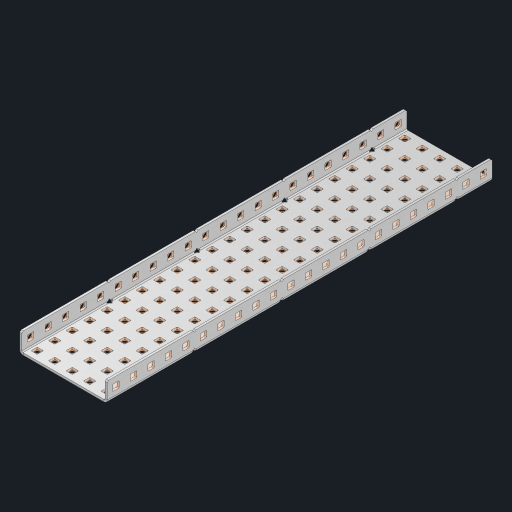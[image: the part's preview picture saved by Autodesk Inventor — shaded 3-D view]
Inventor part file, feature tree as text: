
AUTODESK INVENTOR PART (.ipt)
format: ipt  version: 2023 (Build 270158000, 158)  size: 1,768,448 bytes
history: native  units: in
note: dims shown in document units (in); Inventor stores cm internally (conversion verified against a paired STEP export)
features: other x159, extrude x153, sheet_metal_op x10, sketch x8, mirror x1, pattern_linear x1, chamfer x1
ambient origin geometry x8: Origin, YZ Plane, XZ Plane, XY Plane, X Axis, Y Axis, Z Axis, Center Point
bodies: Solid1 (feature_tree), Body (feature_tree)
feature tree (333):
  other  "Flange Pattern Plane"
  sheet_metal_op  "Flange Pattern"
  sheet_metal_op  "Body Pattern"
  other  "Arc Length"
  mirror  "Notch Mirror"
  pattern_linear  "Notch Pattern"  Spacing1=0.25in  [1 undecoded]
  chamfer  "End Chamfer"
  extrude  "Half Cut"  Depth=0.0625in
  sketch  "Sketch1"  dims[d0=2.5in]
  other  "Plate1"
  sketch  "Sketch2"  dims[d1=11.0in]
  other  "Plate2"
  sheet_metal_op  "Bend1"
  sheet_metal_op  "Corner1"
  sketch  "Sketch3"  dims[d2=0.0625in]
  other  "Flange Pattern Sketch"
  sketch  "Sketch7"  dims[d3=0.0625in]
  other  "Srf1"
  other  "Srf2"
  sketch  "Sketch8"  dims[d4=0.0312in]
  sketch  "Sketch9"  dims[d5=0.125in]
  other  "Srf91"
  sheet_metal_op  "Body Pattern Sketch"
  other  "Srf92"
  sketch  "Sketch13"  dims[d6=0.0625in]
  sketch  "Sketch14"  dims[d7=0.5in d8=90.0deg d9=0.0312in d10=0.25in d11=0.0625in d12=0.0625in d16=0.182in d17=0.02in d18=0.0625in d19=0.0in d20=0.25in d21=0.25in d46=0.172in d47=1.0in d48=0.0in d49=0.182in d50=0.02in d51=0.25in d52=0.25in d53=0.0625in d54=0.0in d55=0.172in d56=1.0in d57=0.0in d60=8.6614in d62=0.5in d63=1.9685in d65=0.5in d85=0.1473in d86=0.1782in d88=0.04in d89=0.0625in d90=0.0in d91=0.04in d92=0.0491in d95=2.5in d96=0.04in d97=0.25in d98=45.0deg d101=0.0in d102=2.497in d131=2.5in d132=8.6614in d134=0.5in d139=0.5in]
  other  "Srf856"
  other  "Srf1310"
  other  "Srf1311"
  other  "Srf1312"
  other  "Srf1376"
  other  "Srf1377"
  other  "Srf1728"
  other  "Srf1755"
  other  "Srf1878"
  other  "Srf1879"
  other  "Srf1880"
  other  "Srf1881"
  other  "Srf1882"
  other  "Srf1883"
  other  "Srf1884"
  other  "Srf1885"
  other  "Srf1886"
  other  "Srf1887"
  other  "Srf1888"
  other  "Srf1889"
  other  "Srf1890"
  other  "Srf1891"
  other  "Srf1892"
  other  "Srf1893"
  other  "Srf1894"
  other  "Srf1895"
  other  "Srf1896"
  other  "Srf1897"
  other  "Srf1898"
  other  "Srf1899"
  other  "Srf1900"
  other  "Srf1901"
  other  "Srf1902"
  other  "Srf1903"
  other  "Srf1904"
  other  "Srf1905"
  other  "Srf1906"
  other  "Srf1942"
  other  "Srf1943"
  other  "Srf1944"
  other  "Srf1945"
  other  "Srf1946"
  other  "Srf1947"
  other  "Srf1948"
  other  "Srf1949"
  other  "Srf1950"
  other  "Srf1951"
  other  "Srf1952"
  other  "Srf1953"
  other  "Srf1954"
  other  "Srf1955"
  other  "Srf1956"
  other  "Srf1957"
  other  "Srf1958"
  other  "Srf1959"
  other  "Srf1960"
  other  "Srf1961"
  other  "Srf1962"
  other  "Srf1963"
  other  "Srf1964"
  other  "Srf1965"
  other  "Srf1966"
  other  "Srf1967"
  other  "Srf1968"
  other  "Srf1969"
  other  "Srf1970"
  other  "Srf2111"
  other  "Srf2112"
  other  "Srf2113"
  other  "Srf2114"
  other  "Srf2115"
  other  "Srf2116"
  other  "Srf2117"
  other  "Srf2118"
  other  "Srf2119"
  other  "Srf2146"
  other  "Srf2147"
  other  "Srf2148"
  other  "Srf2149"
  other  "Srf2150"
  other  "Srf2151"
  other  "Srf2152"
  other  "Srf2153"
  other  "Srf2154"
  other  "Srf2155"
  other  "Srf2156"
  other  "Srf2157"
  other  "Srf2158"
  other  "Srf2159"
  other  "Srf2160"
  other  "Srf2161"
  other  "Srf2162"
  other  "Srf2163"
  other  "Srf2164"
  other  "Srf2165"
  other  "Srf2166"
  other  "Srf2167"
  other  "Srf2168"
  other  "Srf2169"
  other  "Srf2170"
  other  "Srf2171"
  other  "Srf2172"
  other  "Srf2173"
  other  "Srf2174"
  other  "Srf2175"
  other  "Srf2176"
  other  "Srf2177"
  other  "Srf2178"
  other  "Srf2179"
  other  "Srf2180"
  other  "Srf2181"
  other  "Srf2182"
  other  "Srf2183"
  other  "Srf2184"
  other  "Srf2185"
  other  "Srf2186"
  other  "Srf2187"
  other  "Srf2188"
  other  "Srf2189"
  other  "Srf2190"
  other  "Srf2191"
  other  "Srf2192"
  other  "Srf2193"
  other  "Srf2194"
  other  "Srf2195"
  other  "Srf2196"
  other  "Srf2197"
  other  "Srf2198"
  other  "Srf2199"
  other  "Srf2200"
  other  "Srf2201"
  other  "Srf2202"
  other  "Srf2203"
  other  "Srf2204"
  other  "Srf2205"
  other  "Srf2206"
  other  "Srf2207"
  other  "Srf2208"
  other  "Srf2209"
  other  "Srf2210"
  other  "Srf2211"
  other  "Srf2212"
  other  "Srf2213"
  other  "Srf2214"
  other  "Srf2215"
  other  "Srf2216"
  other  "Srf2217"
  other  "Srf2218"
  other  "Srf2219"
  other  "Srf2220"
  sheet_metal_op  "Flange Stamp"
  sheet_metal_op  "Flange Circle"
  sheet_metal_op  "Body Stamp"
  sheet_metal_op  "Body Circle"
  sheet_metal_op  "Notch"
  extrude  "ExtrusionSrf2"  Depth=0.0625in
  extrude  "ExtrusionSrf92"  Depth=2.5in
  extrude  "ExtrusionSrf856"  Depth=0.02in
  extrude  "ExtrusionSrf1310"  Depth=0.0625in
  extrude  "ExtrusionSrf1311"  TaperAngle=0.0deg  [1 undecoded]
  extrude  "ExtrusionSrf1312"  Depth=0.25in
  extrude  "ExtrusionSrf1376"  Depth=0.25in
  extrude  "ExtrusionSrf1377"  Depth=2.5in
  extrude  "ExtrusionSrf1728"  Depth=2.5in TaperAngle=0.0deg
  extrude  "ExtrusionSrf1755"  Depth=2.5in
  extrude  "ExtrusionSrf1878"  Depth=0.02in
  extrude  "ExtrusionSrf1879"  Depth=0.25in
  extrude  "ExtrusionSrf1880"  Depth=0.25in
  extrude  "ExtrusionSrf1881"  Depth=0.0625in
  extrude  "ExtrusionSrf1882"  TaperAngle=0.0deg  [1 undecoded]
  extrude  "ExtrusionSrf1883"  Depth=2.5in
  extrude  "ExtrusionSrf1884"  Depth=2.5in TaperAngle=0.0deg
  extrude  "ExtrusionSrf1885"  Depth=2.5in
  extrude  "ExtrusionSrf1886"  Depth=2.5in
  extrude  "ExtrusionSrf1887"  Depth=2.5in
  extrude  "ExtrusionSrf1888"  Depth=2.5in
  extrude  "ExtrusionSrf1889"  Depth=2.5in
  extrude  "ExtrusionSrf1890"  Depth=0.0625in
  extrude  "ExtrusionSrf1891"  TaperAngle=0.0deg  [1 undecoded]
  extrude  "ExtrusionSrf1892"  Depth=2.5in
  extrude  "ExtrusionSrf1893"  Depth=2.5in
  extrude  "ExtrusionSrf1894"  Depth=2.5in
  extrude  "ExtrusionSrf1895"  Depth=0.25in TaperAngle=45.0deg
  extrude  "ExtrusionSrf1896"  TaperAngle=0.0deg  [1 undecoded]
  extrude  "ExtrusionSrf1897"  Depth=2.5in
  extrude  "ExtrusionSrf1898"  Depth=2.5in
  extrude  "ExtrusionSrf1899"  Depth=2.5in
  extrude  "ExtrusionSrf1900"  Depth=2.5in
  extrude  "ExtrusionSrf1901"  Depth=2.5in
  extrude  "ExtrusionSrf1902"  [1 undecoded]
  extrude  "ExtrusionSrf1903"  [1 undecoded]
  extrude  "ExtrusionSrf1904"  [1 undecoded]
  extrude  "ExtrusionSrf1905"  [1 undecoded]
  extrude  "ExtrusionSrf1906"  [1 undecoded]
  extrude  "ExtrusionSrf1942"  [1 undecoded]
  extrude  "ExtrusionSrf1943"  [1 undecoded]
  extrude  "ExtrusionSrf1944"  [1 undecoded]
  extrude  "ExtrusionSrf1945"  [1 undecoded]
  extrude  "ExtrusionSrf1946"  [1 undecoded]
  extrude  "ExtrusionSrf1947"  [1 undecoded]
  extrude  "ExtrusionSrf1948"  [1 undecoded]
  extrude  "ExtrusionSrf1949"  [1 undecoded]
  extrude  "ExtrusionSrf1950"  [1 undecoded]
  extrude  "ExtrusionSrf1951"  [1 undecoded]
  extrude  "ExtrusionSrf1952"  [1 undecoded]
  extrude  "ExtrusionSrf1953"  [1 undecoded]
  extrude  "ExtrusionSrf1954"  [1 undecoded]
  extrude  "ExtrusionSrf1955"  [1 undecoded]
  extrude  "ExtrusionSrf1956"  [1 undecoded]
  extrude  "ExtrusionSrf1957"  [1 undecoded]
  extrude  "ExtrusionSrf1958"  [1 undecoded]
  extrude  "ExtrusionSrf1959"  [1 undecoded]
  extrude  "ExtrusionSrf1960"  [1 undecoded]
  extrude  "ExtrusionSrf1961"  [1 undecoded]
  extrude  "ExtrusionSrf1962"  [1 undecoded]
  extrude  "ExtrusionSrf1963"  [1 undecoded]
  extrude  "ExtrusionSrf1964"  [1 undecoded]
  extrude  "ExtrusionSrf1965"  [1 undecoded]
  extrude  "ExtrusionSrf1966"  [1 undecoded]
  extrude  "ExtrusionSrf1967"  [1 undecoded]
  extrude  "ExtrusionSrf1968"  [1 undecoded]
  extrude  "ExtrusionSrf1969"  [1 undecoded]
  extrude  "ExtrusionSrf1970"  [1 undecoded]
  extrude  "ExtrusionSrf2111"  [1 undecoded]
  extrude  "ExtrusionSrf2112"  [1 undecoded]
  extrude  "ExtrusionSrf2113"  [1 undecoded]
  extrude  "ExtrusionSrf2114"  [1 undecoded]
  extrude  "ExtrusionSrf2115"  [1 undecoded]
  extrude  "ExtrusionSrf2116"  [1 undecoded]
  extrude  "ExtrusionSrf2117"  [1 undecoded]
  extrude  "ExtrusionSrf2118"  [1 undecoded]
  extrude  "ExtrusionSrf2119"  [1 undecoded]
  extrude  "ExtrusionSrf2146"  [1 undecoded]
  extrude  "ExtrusionSrf2147"  [1 undecoded]
  extrude  "ExtrusionSrf2148"  [1 undecoded]
  extrude  "ExtrusionSrf2149"  [1 undecoded]
  extrude  "ExtrusionSrf2150"  [1 undecoded]
  extrude  "ExtrusionSrf2151"  [1 undecoded]
  extrude  "ExtrusionSrf2152"  [1 undecoded]
  extrude  "ExtrusionSrf2153"  [1 undecoded]
  extrude  "ExtrusionSrf2154"  [1 undecoded]
  extrude  "ExtrusionSrf2155"  [1 undecoded]
  extrude  "ExtrusionSrf2156"  [1 undecoded]
  extrude  "ExtrusionSrf2157"  [1 undecoded]
  extrude  "ExtrusionSrf2158"  [1 undecoded]
  extrude  "ExtrusionSrf2159"  [1 undecoded]
  extrude  "ExtrusionSrf2160"  [1 undecoded]
  extrude  "ExtrusionSrf2161"  [1 undecoded]
  extrude  "ExtrusionSrf2162"  [1 undecoded]
  extrude  "ExtrusionSrf2163"  [1 undecoded]
  extrude  "ExtrusionSrf2164"  [1 undecoded]
  extrude  "ExtrusionSrf2165"  [1 undecoded]
  extrude  "ExtrusionSrf2166"  [1 undecoded]
  extrude  "ExtrusionSrf2167"  [1 undecoded]
  extrude  "ExtrusionSrf2168"  [1 undecoded]
  extrude  "ExtrusionSrf2169"  [1 undecoded]
  extrude  "ExtrusionSrf2170"  [1 undecoded]
  extrude  "ExtrusionSrf2171"  [1 undecoded]
  extrude  "ExtrusionSrf2172"  [1 undecoded]
  extrude  "ExtrusionSrf2173"  [1 undecoded]
  extrude  "ExtrusionSrf2174"  [1 undecoded]
  extrude  "ExtrusionSrf2175"  [1 undecoded]
  extrude  "ExtrusionSrf2176"  [1 undecoded]
  extrude  "ExtrusionSrf2177"  [1 undecoded]
  extrude  "ExtrusionSrf2178"  [1 undecoded]
  extrude  "ExtrusionSrf2179"  [1 undecoded]
  extrude  "ExtrusionSrf2180"  [1 undecoded]
  extrude  "ExtrusionSrf2181"  [1 undecoded]
  extrude  "ExtrusionSrf2182"  [1 undecoded]
  extrude  "ExtrusionSrf2183"  [1 undecoded]
  extrude  "ExtrusionSrf2184"  [1 undecoded]
  extrude  "ExtrusionSrf2185"  [1 undecoded]
  extrude  "ExtrusionSrf2186"  [1 undecoded]
  extrude  "ExtrusionSrf2187"  [1 undecoded]
  extrude  "ExtrusionSrf2188"  [1 undecoded]
  extrude  "ExtrusionSrf2189"  [1 undecoded]
  extrude  "ExtrusionSrf2190"  [1 undecoded]
  extrude  "ExtrusionSrf2191"  [1 undecoded]
  extrude  "ExtrusionSrf2192"  [1 undecoded]
  extrude  "ExtrusionSrf2193"  [1 undecoded]
  extrude  "ExtrusionSrf2194"  [1 undecoded]
  extrude  "ExtrusionSrf2195"  [1 undecoded]
  extrude  "ExtrusionSrf2196"  [1 undecoded]
  extrude  "ExtrusionSrf2197"  [1 undecoded]
  extrude  "ExtrusionSrf2198"  [1 undecoded]
  extrude  "ExtrusionSrf2199"  [1 undecoded]
  extrude  "ExtrusionSrf2200"  [1 undecoded]
  extrude  "ExtrusionSrf2201"  [1 undecoded]
  extrude  "ExtrusionSrf2202"  [1 undecoded]
  extrude  "ExtrusionSrf2203"  [1 undecoded]
  extrude  "ExtrusionSrf2204"  [1 undecoded]
  extrude  "ExtrusionSrf2205"  [1 undecoded]
  extrude  "ExtrusionSrf2206"  [1 undecoded]
  extrude  "ExtrusionSrf2207"  [1 undecoded]
  extrude  "ExtrusionSrf2208"  [1 undecoded]
  extrude  "ExtrusionSrf2209"  [1 undecoded]
  extrude  "ExtrusionSrf2210"  [1 undecoded]
  extrude  "ExtrusionSrf2211"  [1 undecoded]
  extrude  "ExtrusionSrf2212"  [1 undecoded]
  extrude  "ExtrusionSrf2213"  [1 undecoded]
  extrude  "ExtrusionSrf2214"  [1 undecoded]
  extrude  "ExtrusionSrf2215"  [1 undecoded]
  extrude  "ExtrusionSrf2216"  [1 undecoded]
  extrude  "ExtrusionSrf2217"  [1 undecoded]
  extrude  "ExtrusionSrf2218"  [1 undecoded]
  extrude  "ExtrusionSrf2219"  [1 undecoded]
  extrude  "ExtrusionSrf2220"  [1 undecoded]
note: 123 required parameter values undecoded (feature->parameter linkage not recoverable at this tier; creation-order binding heuristic only, values carry confidence <= 0.55)
